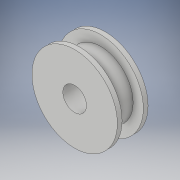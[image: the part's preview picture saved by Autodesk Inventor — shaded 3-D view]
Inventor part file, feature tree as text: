
AUTODESK INVENTOR PART (.ipt)
format: ipt  version: 2019 (Build 230136000, 136)  size: 120,832 bytes
history: native  units: in
note: dims shown in document units (in); Inventor stores cm internally (conversion verified against a paired STEP export)
features: sketch x3, extrude x2, hole x1, mirror x1
ambient origin geometry x8: Origin, YZ Plane, XZ Plane, XY Plane, X Axis, Y Axis, Z Axis, Center Point
bodies: Solid1 (feature_tree)
feature tree (7):
  extrude  "Extrusion1"  Depth=0.04in TaperAngle=0.0deg
  extrude  "Extrusion2"  Depth=0.09in TaperAngle=0.0deg
  hole  "Hole1"  [1 undecoded]
  mirror  "Mirror1"
  sketch  "Sketch1"  dims[d0=0.723in d1=0.04in d2=0.0in]
  sketch  "Sketch2"  dims[d3=0.55in d4=0.09in d5=0.0in]
  sketch  "Sketch3"  dims[d6=0.2in d7=0.75in d8=0.375in d9=0.25in d10=0.5635in d11=1.0in d12=0.8108in]
note: 1 required parameter value undecoded (feature->parameter linkage not recoverable at this tier; creation-order binding heuristic only, values carry confidence <= 0.55)
